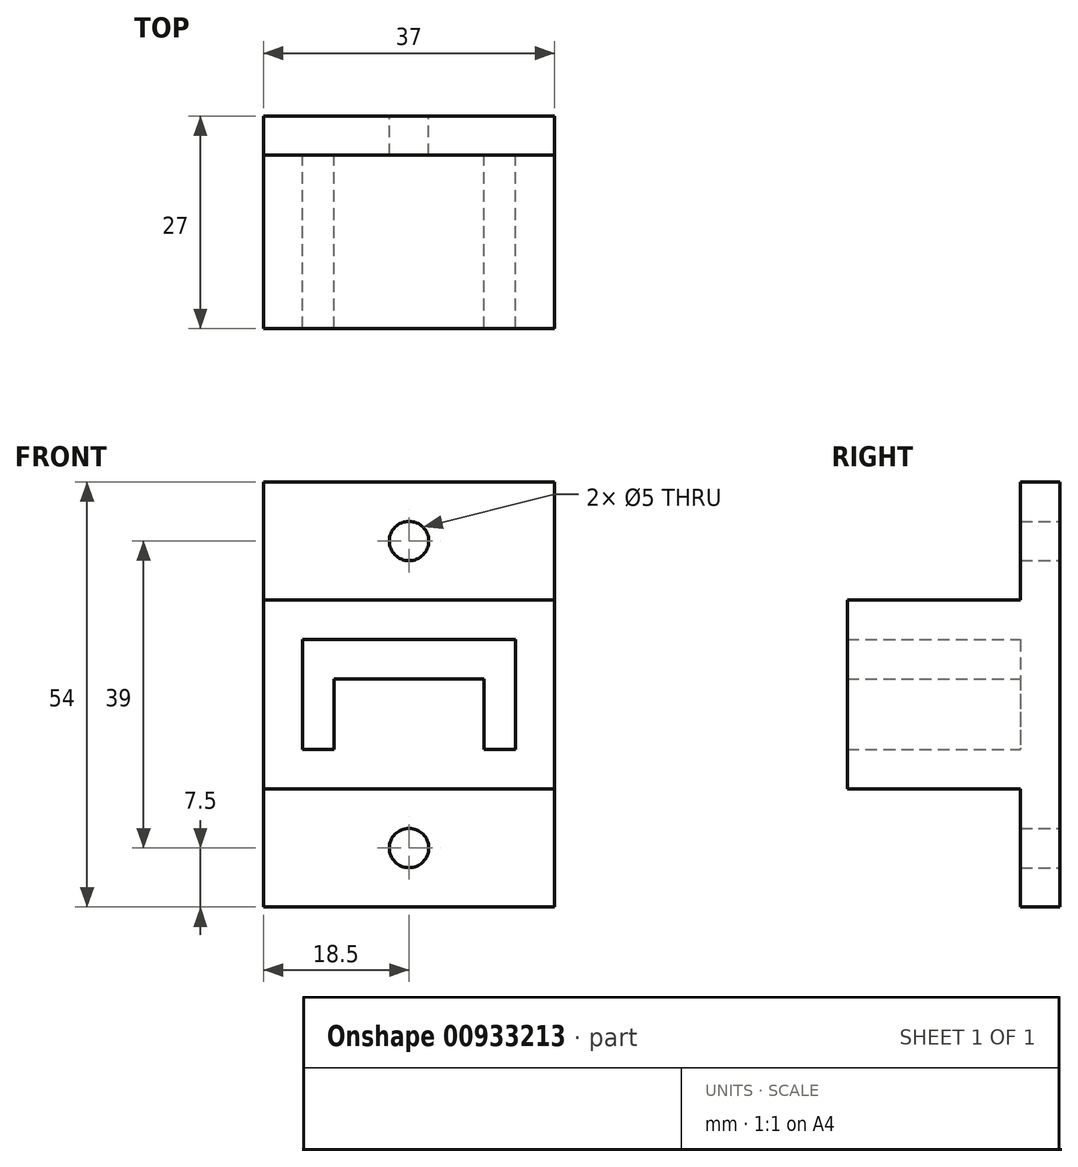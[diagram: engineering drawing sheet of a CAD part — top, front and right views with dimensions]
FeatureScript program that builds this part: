
annotation { "Feature Type Name" : "Feature", "Feature Type Description" : "" }
export const myFeature = defineFeature(function(context is Context, id is Id, definition is map)
    precondition{}
    {
        {
            var Q0;
            Q0=qCreatedBy(makeId("Front.planeOp"),FACE);
            var sketch = newSketch(context, id + "F0", { "sketchPlane" : qUnion([Q0])});
            skLineSegment(sketch, "E0", {"start": v(0, 0) * mm, "end": v(27, 0) * mm});
            skLineSegment(sketch, "E1", {"start": v(0, 0) * mm, "end": v(0, -14) * mm});
            skLineSegment(sketch, "E2", {"start": v(0, -14) * mm, "end": v(4, -14) * mm});
            skLineSegment(sketch, "E3", {"start": v(4, -14) * mm, "end": v(4, -5) * mm});
            skLineSegment(sketch, "E4", {"start": v(4, -5) * mm, "end": v(23, -5) * mm});
            skLineSegment(sketch, "E5", {"start": v(23, -5) * mm, "end": v(23, -14) * mm});
            skLineSegment(sketch, "E6", {"start": v(23, -14) * mm, "end": v(27, -14) * mm});
            skLineSegment(sketch, "E7", {"start": v(27, -14) * mm, "end": v(27, 0) * mm});
            skLineSegment(sketch, "E8", {"start": v(32, 5) * mm, "end": v(32, -19) * mm});
            skLineSegment(sketch, "E9", {"start": v(32, 5) * mm, "end": v(-5, 5) * mm});
            skLineSegment(sketch, "E10", {"start": v(-5, 5) * mm, "end": v(-5, -19) * mm});
            skLineSegment(sketch, "E11", {"start": v(-5, -19) * mm, "end": v(32, -19) * mm});
            skSolve(sketch);
        }
        {
            var Q0;
            Q0=makeQuery(id+"F0.imprint","IMPRINT",FACE,{"disambiguationData":[TD([[makeQuery(id+"F0.imprint","IMPRINT",EDGE,{"derivedFrom":sQuery(id+"F0.wireOp",EDGE,"E0")}),1.0]])]});
            extrude(context, id + "F1", {"entities" : qUnion([Q0]), "depth" : 27 * mm, "offsetDistance" : 25 * mm});
        }
        {
            var Q0;
            Q0=qCreatedBy(makeId("Front.planeOp"),FACE);
            var sketch = newSketch(context, id + "F2", { "sketchPlane" : qUnion([Q0])});
            skLineSegment(sketch, "E12", {"start": v(-5, 20) * mm, "end": v(-5, -34) * mm});
            skLineSegment(sketch, "E13", {"start": v(-5, 20) * mm, "end": v(32, 20) * mm});
            skLineSegment(sketch, "E14", {"start": v(32, 20) * mm, "end": v(32, -34) * mm});
            skLineSegment(sketch, "E15", {"start": v(-5, -34) * mm, "end": v(32, -34) * mm});
            skCircle(sketch, "E16", {"center": v(13.5, 12.5) * mm, "radius": 2.5 * mm});
            skCircle(sketch, "E17", {"center": v(13.5, -26.5) * mm, "radius": 2.5 * mm});
            skSolve(sketch);
        }
        {
            var Q0;
            Q0=makeQuery(id+"F2.imprint","IMPRINT",FACE,{"disambiguationData":[TD([[makeQuery(id+"F2.imprint","IMPRINT",EDGE,{"derivedFrom":sQuery(id+"F2.wireOp",EDGE,"E12")}),1.0]])]});
            extrude(context, id + "F3", {"entities" : qUnion([Q0]), "operationType" : NewBodyOperationType.ADD, "depth" : 5 * mm, "offsetDistance" : 25 * mm});
        }
    });
